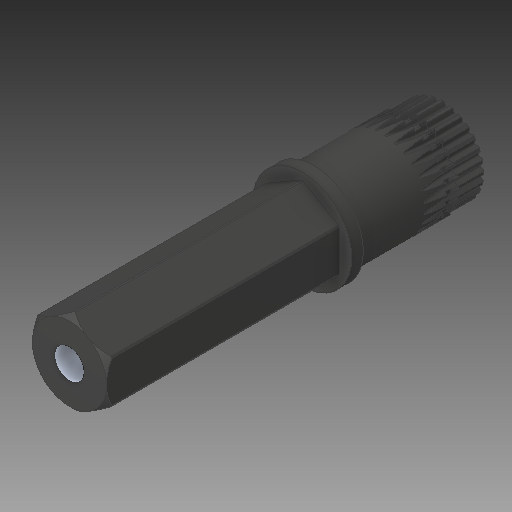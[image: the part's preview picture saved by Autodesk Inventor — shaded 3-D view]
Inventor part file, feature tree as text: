
AUTODESK INVENTOR PART (.ipt)
format: ipt  version: 2018 (Build 220112000, 112)  size: 1,423,872 bytes
history: native  units: in
note: dims shown in document units (in); Inventor stores cm internally (conversion verified against a paired STEP export)
features: fillet x1
ambient origin geometry x8: Origin, YZ Plane, XZ Plane, XY Plane, X Axis, Y Axis, Z Axis, Center Point
bodies: Solid1 (feature_tree)
feature tree (1):
  fillet  "Fillet5"  [1 undecoded]
note: 1 required parameter value undecoded (feature->parameter linkage not recoverable at this tier; creation-order binding heuristic only, values carry confidence <= 0.55)
